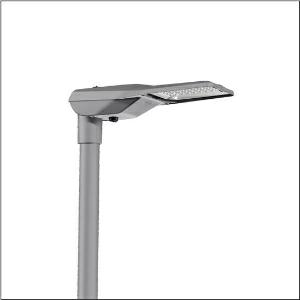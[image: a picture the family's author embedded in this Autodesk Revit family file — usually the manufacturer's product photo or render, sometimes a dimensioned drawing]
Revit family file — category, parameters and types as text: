
# Revit family: streetlight_sl_21_iq_mini___st1_0a_5xe2d31y08jb_55ca
name_source: partatom
category: Lighting Fixtures
units: mm (PartAtom-declared; Revit-internal decimal feet)

## family parameters
Cut with Voids When Loaded = No
Host = Face
Light Source = No
Part Type = Normal
Room Calculation Point = No
Round Connector Dimension = Use Diameter
Shared = No

## types (1)
- --- (1 x LED, 11210 lm, 72.5 W, 3000K)
    Apparent Load = 73 VA
    CIE Flux Codes = 40 73 97 100 100
    Color Rendering = 70
    Color Temperature = 3000K
    Default Elevation = 1800 mm
    Description = Streetlight SL 21 iQ mini, mast luminaire, primary light control with lens, of PMMA, primary optical cover: cover, of toughened safety glass, transparent, light distribution: ST1.0a, light emission: direct distribution, primary light characteristic: asymmetric, installation type: post-top, side-entry, LED, High Power LED, rated luminous flux: 11.210lm, luminous efficacy: 155lm/W, light colour: 730, colour temperature: 3000K, control: presetting dimming logarithmic, Street-Remote, Auto-Match, Temp-Guard, Lumen-Switch, Night-Set, Smart-Wire, Light-Fading, Desk-Remote (wireless, voltage-free reading and setting of iQ features in the workshop via application-optimized NFC function/RFID function), optimised constant luminous flux control (CLO 2.0), mains connection: 220..240V, AC, 50/60Hz, start of lifetime: 73W, end of service life: 76W, reduction: 33W, luminaire housing, of diecast aluminium, powder-coated, Siteco® metallic grey (DB 702S), corrosivity category C5 mid according to DIN EN ISO 12944, please order mast flange separately, inclination adjustable: 0°, 5°, 10°, 15°, sealing non-destructively replaceable, multi-level sealing system, length: 628mm, width: 235mm, height: 110mm, mast flange for spigot size: 42mm (side-entry): 5XC10008XM4, 60/48mm (side-entry/post-top): 5XC10108XM2, 76/60mm (side-entry/post-top): 5XC10108XM1, Smart Interface below and above, protection rating (complete): IP66, insulation class (complete): insulation class II (safety insulation), certification: CE, ENEC, ENEC+, VDE, impact resistance: IK09, permissible operating ambient temperature for outdoor applications: -40..+50°C, standard-compliant lighting for roads and squares, packaging unit: 1 piece

Light Distribution: ST1.0a
    Height = 110 mm
    Lamp = 1 x LED
    Lamp Light Flux = 11210 lm
    Lamp Power = 72.5 W
    Lamp count = 1
    Length = 625 mm
    Luminous efficacy = 155 lm/W
    Manufacturer = Siteco
    ModVariant = No
    Model = 5XE2D31Y08JB
    Number of Poles = 1
    OnlyDefault = Yes
    Power Factor = 1
    Product Name = Streetlight SL 21 iQ mini | ST1.0a
    Product group = mast luminaire | pylon top
    ProductGroupID = 6100
    Protection Class = Protection class II
    Protection Degree = IP 66
    RLX_Detail_Level = 1
    RLX_Emergency_Light_Flux = 0 lm
    RLX_Emergency_Type = 0
    RLX_Emergency_Type_DB = No
    RlxData = <blob elided: 92809 chars, md5=13ed4f56>
    Socket = socket
    Standby Power = 0 W
    System Light Flux = 11210 lm
    System Power = 73 W
    Type Comments = factory setting: luminous flux: 100 % | dim-lin: 254 | 755 mA
    Type Image = l_1003514.jpg
    URL = http://relux.com
    VarID = @adj_062269
    Voltage = 0 V
    Weight = 0.00 kg
    Width = 234 mm

## geometry (parser evidence)
native form markers: Blend x4, Sweep x11
no freeform markers — native parametric forms only
